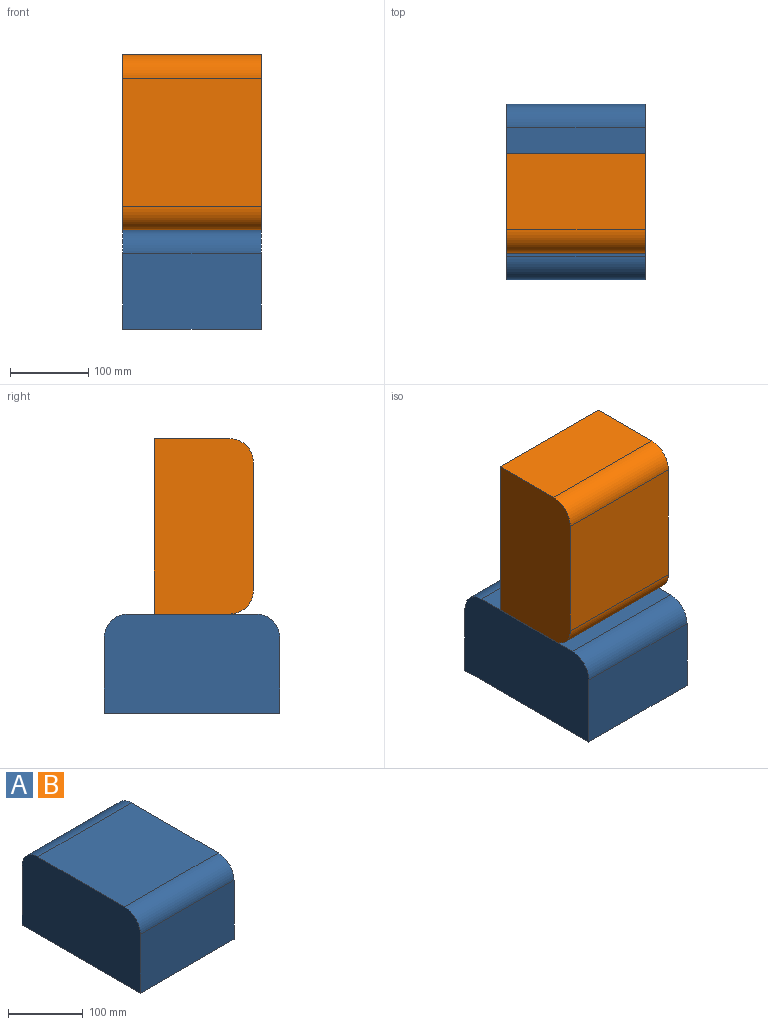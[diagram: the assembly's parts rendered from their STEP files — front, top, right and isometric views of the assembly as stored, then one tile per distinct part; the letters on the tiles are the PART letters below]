
ASSEMBLY  parts=2 mates=1
PART A: 8 faces, bbox 177.8x224.5x127 mm
  f0: plane 177.8x164.44mm, normal (0,0,1), area 29237.7mm2, adj f1,f3,f6,f7
  f1: plane 224.54x127mm, normal (-1,0,0), area 28128.6mm2, adj f0,f2,f4,f5,f6,f7
  f2: plane 224.54x177.8mm, normal (0,0,-1), area 39922.5mm2, adj f1,f3,f4,f5
  f3: plane 224.54x127mm, normal (1,0,0), area 28128.6mm2, adj f0,f2,f4,f5,f6,f7
  f4: plane 177.8x96.95mm, normal (0,-1,0), area 17238.2mm2, adj f1,f2,f3,f7
  f5: plane 177.8x96.95mm, normal (0,1,0), area 17238.2mm2, adj f1,f2,f3,f6
  f6: cylinder r=30.05mm len=177.8mm, axis (-1,0,0), area 8391.8mm2, adj f0,f1,f3,f5
  f7: cylinder r=30.05mm len=177.8mm, axis (1,0,0), area 8391.8mm2, adj f0,f1,f3,f4
PART B: same geometry as A
PLACE A t=(132.16,180.92,-28.36)mm
PLACE B rot(axis=(1,0,0),90deg) t=(132.16,74.84,280.89)mm
MATE planar B.f4 <-> A.f0  axis (0,0,-1) through (127.16,68.65,56.35)mm
